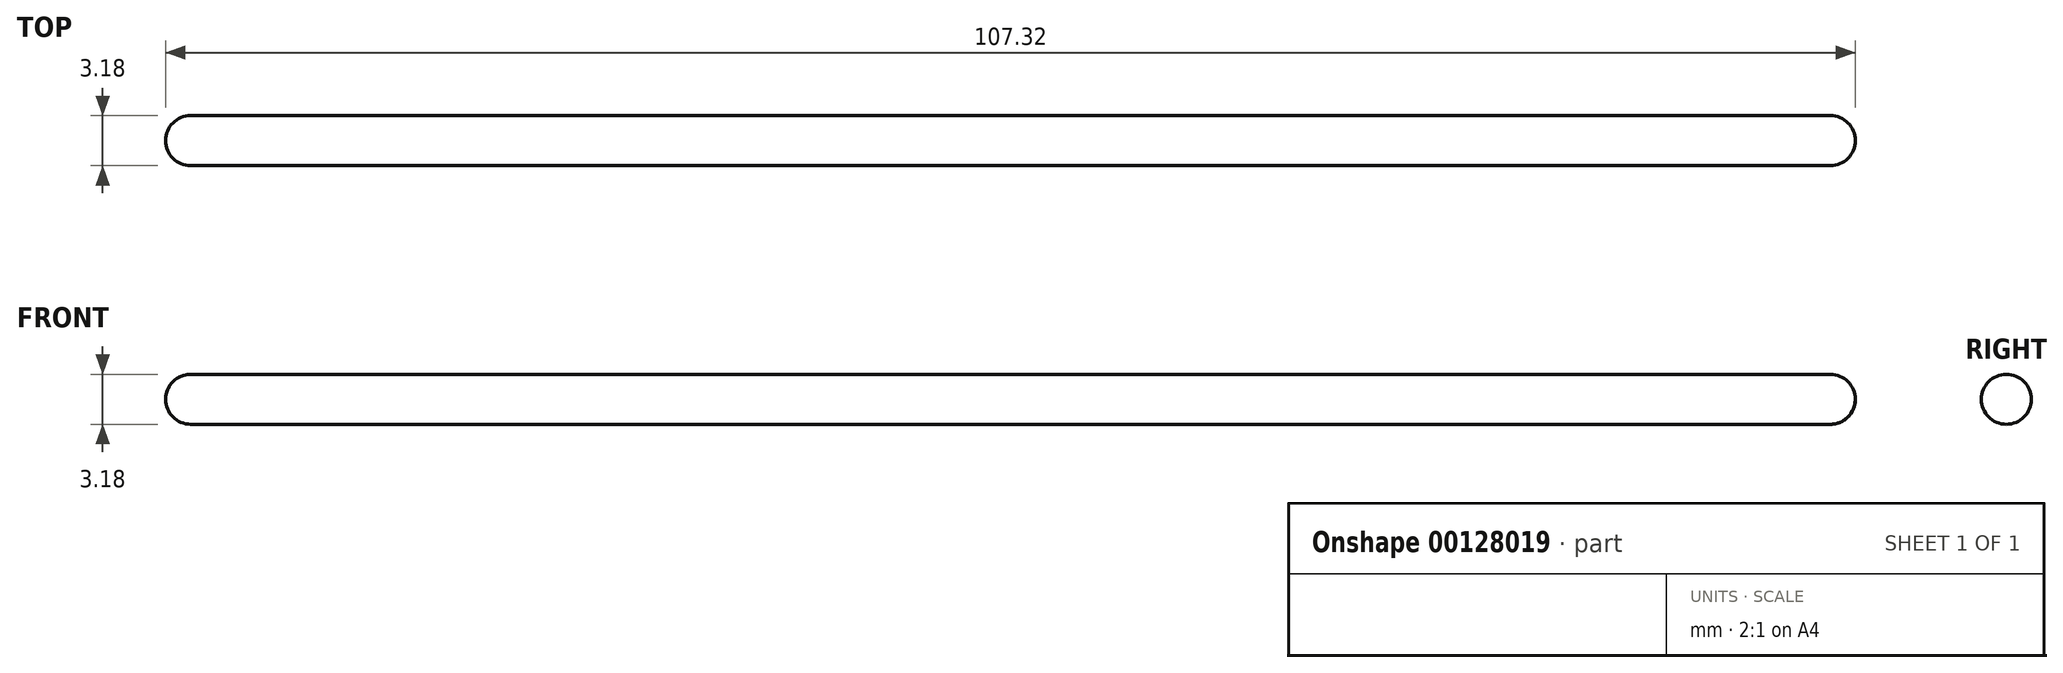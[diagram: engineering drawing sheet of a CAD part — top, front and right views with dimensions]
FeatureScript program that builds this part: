
annotation { "Feature Type Name" : "Feature", "Feature Type Description" : "" }
export const myFeature = defineFeature(function(context is Context, id is Id, definition is map)
    precondition{}
    {
        {
            var Q0;
            Q0=qCreatedBy(makeId("Front.planeOp"),FACE);
            var sketch = newSketch(context, id + "F0", { "sketchPlane" : qUnion([Q0])});
            skLineSegment(sketch, "E0", {"start": v(-52.07, 0) * mm, "end": v(52.07, 0) * mm});
            skArc(sketch, "E1", {"start": v(53.66, 0) * mm, "mid": v(53.2, 1.12) * mm, "end": v(52.07, 1.59) * mm});
            skArc(sketch, "E2", {"start": v(-52.07, 1.59) * mm, "mid": v(-53.2, 1.12) * mm, "end": v(-53.66, 0) * mm});
            skLineSegment(sketch, "E3", {"start": v(-52.07, 1.59) * mm, "end": v(52.07, 1.59) * mm});
            skLineSegment(sketch, "E4", {"start": v(-52.07, 0) * mm, "end": v(-53.66, 0) * mm});
            skLineSegment(sketch, "E5", {"start": v(-53.66, 0) * mm, "end": v(53.66, 0) * mm});
            skSolve(sketch);
        }
        {
            var Q0;
            {var subQ0=sQuery(id+"F0.wireOp",EDGE,"E1");Q0=makeQuery(id+"F0.imprint","IMPRINT",FACE,{"disambiguationData":[TD([[makeQuery(id+"F0.imprint","IMPRINT",EDGE,{"derivedFrom":subQ0}),1.0]])]});}
            var Q1;
            Q1=sQuery(id+"F0.wireOp",EDGE,"E5");
            revolve(context, id + "F1", {"entities" : qUnion([Q0]), "axis" : qUnion([Q1]), "revolveType" : RevolveType.FULL});
        }
    });
